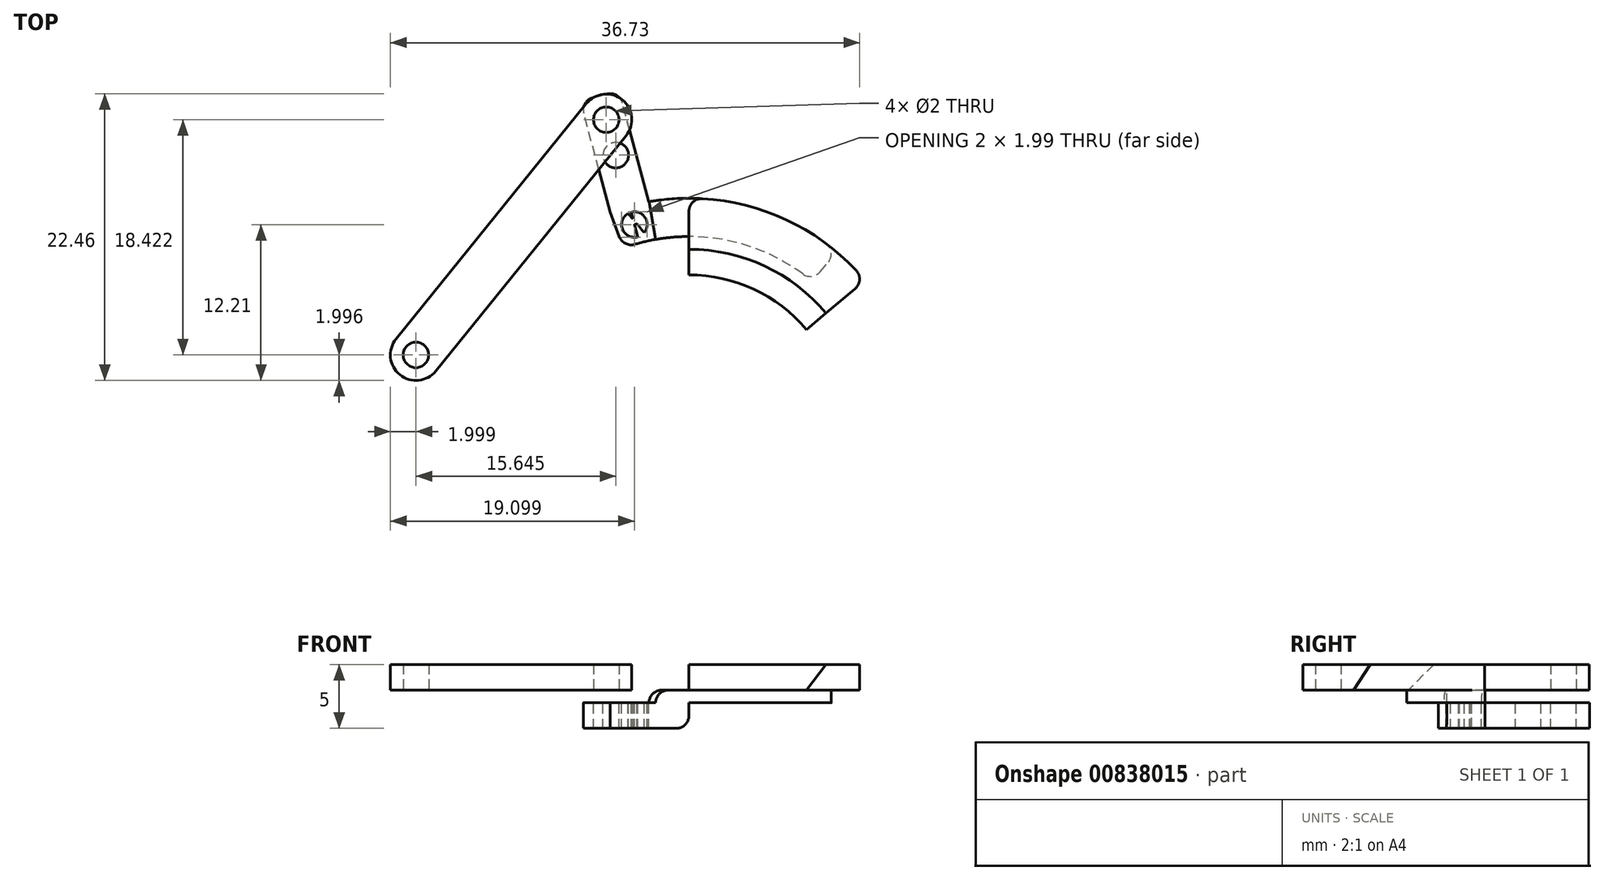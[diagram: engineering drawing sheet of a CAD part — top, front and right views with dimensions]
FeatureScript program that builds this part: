
annotation { "Feature Type Name" : "Feature", "Feature Type Description" : "" }
export const myFeature = defineFeature(function(context is Context, id is Id, definition is map)
    precondition{}
    {
        {
            var Q0;
            Q0=qCreatedBy(makeId("Top.planeOp"),FACE);
            var sketch = newSketch(context, id + "F0", { "sketchPlane" : qUnion([Q0])});
            skCircle(sketch, "E0", {"center": v(0, 0) * mm, "radius": 12 * mm});
            skLineSegment(sketch, "E1", {"start": v(0, 0) * mm, "end": v(0, 18) * mm});
            skLineSegment(sketch, "E2.1.0", {"start": v(0, 0) * mm, "end": v(-15.59, 9) * mm});
            skLineSegment(sketch, "E2.2.0", {"start": v(0, 0) * mm, "end": v(-15.59, -9) * mm});
            skLineSegment(sketch, "E2.3.0", {"start": v(0, 0) * mm, "end": v(0, -18) * mm});
            skLineSegment(sketch, "E2.4.0", {"start": v(0, 0) * mm, "end": v(15.59, -9) * mm});
            skLineSegment(sketch, "E2.5.0", {"start": v(0, 0) * mm, "end": v(15.59, 9) * mm});
            skLineSegment(sketch, "E3", {"start": v(0, 0) * mm, "end": v(-3.13, 17.73) * mm});
            skLineSegment(sketch, "E4.1.0", {"start": v(0, 0) * mm, "end": v(-16.91, 6.16) * mm});
            skLineSegment(sketch, "E4.2.0", {"start": v(0, 0) * mm, "end": v(-13.79, -11.57) * mm});
            skLineSegment(sketch, "E4.3.0", {"start": v(0, 0) * mm, "end": v(3.13, -17.73) * mm});
            skLineSegment(sketch, "E4.4.0", {"start": v(0, 0) * mm, "end": v(16.91, -6.16) * mm});
            skLineSegment(sketch, "E4.5.0", {"start": v(0, 0) * mm, "end": v(13.79, 11.57) * mm});
            skCircle(sketch, "E5", {"center": v(0, 0) * mm, "radius": 18 * mm});
            skLineSegment(sketch, "E6", {"start": v(0, 0) * mm, "end": v(-6.16, 16.91) * mm});
            skCircle(sketch, "E7", {"center": v(0, 0) * mm, "radius": 15 * mm});
            skLineSegment(sketch, "E8", {"start": v(0, 0) * mm, "end": v(11.57, 13.79) * mm});
            skSolve(sketch);
        }
        {
            var Q0;
            {var subQ0=sQuery(id+"F0.wireOp",EDGE,"E4.5.0");var subQ1=sQuery(id+"F0.wireOp",EDGE,"E0");var subQ2=makeQuery(id+"F0.imprint","INTERSECT",VERTEX,{"derivedFrom":[subQ1,subQ0]});Q0=makeQuery(id+"F0.imprint","IMPRINT",FACE,{"disambiguationData":[TD([[makeQuery(id+"F0.imprint","IMPRINT",EDGE,{"disambiguationData":[TD([[subQ2,-1.0]])],"derivedFrom":subQ1}),-1.0]])]});}
            var Q1;
            {var subQ0=sQuery(id+"F0.wireOp",EDGE,"E5");var subQ1=sQuery(id+"F0.wireOp",EDGE,"E1");var subQ2=makeQuery(id+"F0.imprint","INTERSECT",VERTEX,{"derivedFrom":[subQ1,subQ0]});Q1=makeQuery(id+"F0.imprint","IMPRINT",FACE,{"disambiguationData":[TD([[makeQuery(id+"F0.imprint","IMPRINT",EDGE,{"disambiguationData":[TD([[subQ2,1.0]])],"derivedFrom":subQ1}),-1.0]])]});}
            var Q2;
            {var subQ0=sQuery(id+"F0.wireOp",EDGE,"E8");var subQ1=sQuery(id+"F0.wireOp",EDGE,"E0");var subQ2=makeQuery(id+"F0.imprint","INTERSECT",VERTEX,{"derivedFrom":[subQ1,subQ0]});Q2=makeQuery(id+"F0.imprint","IMPRINT",FACE,{"disambiguationData":[TD([[makeQuery(id+"F0.imprint","IMPRINT",EDGE,{"disambiguationData":[TD([[subQ2,-1.0]])],"derivedFrom":subQ1}),-1.0]])]});}
            var Q3;
            {var subQ0=sQuery(id+"F0.wireOp",EDGE,"E5");var subQ1=sQuery(id+"F0.wireOp",EDGE,"E4.5.0");var subQ2=makeQuery(id+"F0.imprint","INTERSECT",VERTEX,{"derivedFrom":[subQ1,subQ0]});Q3=makeQuery(id+"F0.imprint","IMPRINT",FACE,{"disambiguationData":[TD([[makeQuery(id+"F0.imprint","IMPRINT",EDGE,{"disambiguationData":[TD([[subQ2,1.0]])],"derivedFrom":subQ1}),1.0]])]});}
            extrude(context, id + "F1", {"entities" : qUnion([Q0, Q1, Q2, Q3]), "depth" : 2 * mm, "offsetDistance" : 25 * mm});
        }
        {
            var Q0;
            {var subQ0=sQuery(id+"F0.wireOp",EDGE,"E5");var subQ1=sQuery(id+"F0.wireOp",EDGE,"E1");var subQ2=makeQuery(id+"F0.imprint","INTERSECT",VERTEX,{"derivedFrom":[subQ1,subQ0]});Q0=makeQuery(id+"F0.imprint","IMPRINT",FACE,{"disambiguationData":[TD([[makeQuery(id+"F0.imprint","IMPRINT",EDGE,{"disambiguationData":[TD([[subQ2,1.0]])],"derivedFrom":subQ1}),1.0]])]});}
            var Q1;
            {var subQ0=sQuery(id+"F0.wireOp",EDGE,"E5");var subQ1=sQuery(id+"F0.wireOp",EDGE,"E1");var subQ2=makeQuery(id+"F0.imprint","INTERSECT",VERTEX,{"derivedFrom":[subQ1,subQ0]});Q1=makeQuery(id+"F0.imprint","IMPRINT",FACE,{"disambiguationData":[TD([[makeQuery(id+"F0.imprint","IMPRINT",EDGE,{"disambiguationData":[TD([[subQ2,1.0]])],"derivedFrom":subQ1}),-1.0]])]});}
            extrude(context, id + "F2", {"entities" : qUnion([Q0, Q1]), "operationType" : NewBodyOperationType.ADD, "oppositeDirection" : true, "depth" : 1 * mm, "offsetDistance" : 25 * mm});
        }
        {
            var Q0;
            {var subQ0=sQuery(id+"F0.wireOp",EDGE,"E5");var subQ1=sQuery(id+"F0.wireOp",EDGE,"E3");var subQ2=makeQuery(id+"F0.imprint","INTERSECT",VERTEX,{"derivedFrom":[subQ1,subQ0]});Q0=makeQuery(id+"F0.imprint","IMPRINT",FACE,{"disambiguationData":[TD([[makeQuery(id+"F0.imprint","IMPRINT",EDGE,{"disambiguationData":[TD([[subQ2,1.0]])],"derivedFrom":subQ1}),1.0]])]});}
            var Q1;
            {var subQ0=sQuery(id+"F0.wireOp",EDGE,"E5");var subQ1=sQuery(id+"F0.wireOp",EDGE,"E1");var subQ2=makeQuery(id+"F0.imprint","INTERSECT",VERTEX,{"derivedFrom":[subQ1,subQ0]});Q1=makeQuery(id+"F0.imprint","IMPRINT",FACE,{"disambiguationData":[TD([[makeQuery(id+"F0.imprint","IMPRINT",EDGE,{"disambiguationData":[TD([[subQ2,1.0]])],"derivedFrom":subQ1}),1.0]])]});}
            extrude(context, id + "F3", {"entities" : qUnion([Q0, Q1]), "operationType" : NewBodyOperationType.ADD, "oppositeDirection" : true, "depth" : 3 * mm, "offsetDistance" : 25 * mm, "hasSecondDirection" : true, "secondDirectionOppositeDirection" : true, "secondDirectionDepth" : 1 * mm});
        }
        {
            var Q0;
            Q0=qCreatedBy(makeId("Top.planeOp"),FACE);
            var sketch = newSketch(context, id + "F4", { "sketchPlane" : qUnion([Q0])});
            skLineSegment(sketch, "E9", {"start": v(0, 0) * mm, "end": v(-6.47, 24.15) * mm});
            skCircle(sketch, "E10", {"center": v(0, 0) * mm, "radius": 16.5 * mm});
            skCircle(sketch, "E11", {"center": v(-4.27, 15.94) * mm, "radius": 1 * mm});
            skLineSegment(sketch, "E12", {"start": v(0, 0) * mm, "end": v(-24.15, 6.47) * mm});
            skCircle(sketch, "E13", {"center": v(-4.27, 15.94) * mm, "radius": 8.5 * mm});
            skCircle(sketch, "E14", {"center": v(-15.94, 4.27) * mm, "radius": 8.5 * mm});
            skLineSegment(sketch, "E15", {"start": v(-4.27, 15.94) * mm, "end": v(-11.63, 20.19) * mm});
            skLineSegment(sketch, "E16", {"start": v(-15.94, 4.27) * mm, "end": v(-23.3, 0.02) * mm});
            skCircle(sketch, "E17", {"center": v(-23.3, 0.02) * mm, "radius": 25 * mm});
            skCircle(sketch, "E18", {"center": v(-24.15, 6.47) * mm, "radius": 25 * mm});
            skCircle(sketch, "E19", {"center": v(-4.27, 15.94) * mm, "radius": 5.62 * mm});
            skLineSegment(sketch, "E20", {"start": v(-9.14, 18.75) * mm, "end": v(-8.2, 19.95) * mm});
            skLineSegment(sketch, "E21", {"start": v(-5.73, 21.37) * mm, "end": v(-4.22, 21.56) * mm});
            skCircle(sketch, "E22", {"center": v(-5.73, 21.37) * mm, "radius": 1 * mm});
            skCircle(sketch, "E23", {"center": v(-6.47, 24.15) * mm, "radius": 1 * mm});
            skLineSegment(sketch, "E24", {"start": v(0, 0) * mm, "end": v(-7.22, 26.96) * mm});
            skCircle(sketch, "E25", {"center": v(0, 0) * mm, "radius": 18 * mm});
            skLineSegment(sketch, "E26", {"start": v(-6.16, 16.91) * mm, "end": v(-8.49, 25.6) * mm});
            skLineSegment(sketch, "E27", {"start": v(-3.14, 17.72) * mm, "end": v(-5.47, 26.42) * mm});
            skLineSegment(sketch, "E28", {"start": v(-8.49, 25.6) * mm, "end": v(-5.47, 26.42) * mm});
            skCircle(sketch, "E29.1.0", {"center": v(-21.37, 5.73) * mm, "radius": 1 * mm});
            skCircle(sketch, "E29.2.0", {"center": v(-15.64, -15.64) * mm, "radius": 1 * mm});
            skCircle(sketch, "E29.3.0", {"center": v(5.73, -21.37) * mm, "radius": 1 * mm});
            skCircle(sketch, "E29.4.0", {"center": v(21.37, -5.73) * mm, "radius": 1 * mm});
            skCircle(sketch, "E29.5.0", {"center": v(15.64, 15.64) * mm, "radius": 1 * mm});
            skCircle(sketch, "E30", {"center": v(-21.37, 5.73) * mm, "radius": 1.69 * mm});
            skSolve(sketch);
        }
        {
            var Q0;
            {var subQ1=sQuery(id+"F4.wireOp",EDGE,"E27");var subQ3=sQuery(id+"F4.wireOp",EDGE,"E13");var subQ4=makeQuery(id+"F4.imprint","INTERSECT",VERTEX,{"derivedFrom":[subQ3,subQ1]});Q0=makeQuery(id+"F4.imprint","IMPRINT",FACE,{"disambiguationData":[TD([[makeQuery(id+"F4.imprint","IMPRINT",EDGE,{"disambiguationData":[TD([[subQ4,-1.0]])],"derivedFrom":subQ3}),-1.0]])]});}
            var Q1;
            {var subQ0=sQuery(id+"F4.wireOp",EDGE,"E28");var subQ1=sQuery(id+"F4.wireOp",EDGE,"E18");var subQ2=makeQuery(id+"F4.imprint","INTERSECT",VERTEX,{"derivedFrom":[subQ1,subQ0]});Q1=makeQuery(id+"F4.imprint","IMPRINT",FACE,{"disambiguationData":[TD([[makeQuery(id+"F4.imprint","IMPRINT",EDGE,{"disambiguationData":[TD([[subQ2,1.0]])],"derivedFrom":subQ1}),-1.0]])]});}
            var Q2;
            {var subQ3=sQuery(id+"F4.wireOp",EDGE,"E13");var subQ5=sQuery(id+"F4.wireOp",EDGE,"E23");var subQ6=makeQuery(id+"F4.imprint","INTERSECT",VERTEX,{"disambiguationData":[OD(1.0)],"derivedFrom":[subQ3,subQ5]});Q2=makeQuery(id+"F4.imprint","IMPRINT",FACE,{"disambiguationData":[TD([[makeQuery(id+"F4.imprint","IMPRINT",EDGE,{"disambiguationData":[TD([[subQ6,-1.0]])],"derivedFrom":subQ3}),-1.0]])]});}
            var Q3;
            {var subQ5=sQuery(id+"F4.wireOp",EDGE,"E23");var subQ6=sQuery(id+"F4.wireOp",EDGE,"E13");var subQ7=makeQuery(id+"F4.imprint","INTERSECT",VERTEX,{"disambiguationData":[OD(1.0)],"derivedFrom":[subQ6,subQ5]});Q3=makeQuery(id+"F4.imprint","IMPRINT",FACE,{"disambiguationData":[TD([[makeQuery(id+"F4.imprint","IMPRINT",EDGE,{"disambiguationData":[TD([[subQ7,-1.0]])],"derivedFrom":subQ6}),1.0]])]});}
            var Q4;
            {var subQ3=sQuery(id+"F4.wireOp",EDGE,"E25");var subQ5=sQuery(id+"F4.wireOp",EDGE,"E17");var subQ6=makeQuery(id+"F4.imprint","INTERSECT",VERTEX,{"disambiguationData":[OD(1.0)],"derivedFrom":[subQ5,subQ3]});Q4=makeQuery(id+"F4.imprint","IMPRINT",FACE,{"disambiguationData":[TD([[makeQuery(id+"F4.imprint","IMPRINT",EDGE,{"disambiguationData":[TD([[subQ6,-1.0]])],"derivedFrom":subQ5}),-1.0]])]});}
            var Q5;
            {var subQ0=sQuery(id+"F4.wireOp",EDGE,"E25");var subQ1=sQuery(id+"F4.wireOp",EDGE,"E15");var subQ2=makeQuery(id+"F4.imprint","INTERSECT",VERTEX,{"derivedFrom":[subQ1,subQ0]});Q5=makeQuery(id+"F4.imprint","IMPRINT",FACE,{"disambiguationData":[TD([[makeQuery(id+"F4.imprint","IMPRINT",EDGE,{"disambiguationData":[TD([[subQ2,-1.0]])],"derivedFrom":subQ1}),-1.0]])]});}
            var Q6;
            {var subQ1=sQuery(id+"F4.wireOp",EDGE,"E22");var subQ5=sQuery(id+"F4.wireOp",EDGE,"E21");var subQ6=makeQuery(id+"F4.imprint","INTERSECT",VERTEX,{"derivedFrom":[subQ5,subQ1]});Q6=makeQuery(id+"F4.imprint","IMPRINT",FACE,{"disambiguationData":[TD([[makeQuery(id+"F4.imprint","IMPRINT",EDGE,{"disambiguationData":[TD([[subQ6,1.0]])],"derivedFrom":subQ1}),-1.0]])]});}
            var Q7;
            {var subQ1=sQuery(id+"F4.wireOp",EDGE,"E13");var subQ7=sQuery(id+"F4.wireOp",EDGE,"E27");var subQ9=makeQuery(id+"F4.imprint","INTERSECT",VERTEX,{"derivedFrom":[subQ1,subQ7]});Q7=makeQuery(id+"F4.imprint","IMPRINT",FACE,{"disambiguationData":[TD([[makeQuery(id+"F4.imprint","IMPRINT",EDGE,{"disambiguationData":[TD([[subQ9,-1.0]])],"derivedFrom":subQ1}),1.0]])]});}
            var Q8;
            {var subQ5=sQuery(id+"F4.wireOp",EDGE,"E22");var subQ6=sQuery(id+"F4.wireOp",EDGE,"E19");var subQ7=makeQuery(id+"F4.imprint","INTERSECT",VERTEX,{"disambiguationData":[OD(0.0)],"derivedFrom":[subQ6,subQ5]});Q8=makeQuery(id+"F4.imprint","IMPRINT",FACE,{"disambiguationData":[TD([[makeQuery(id+"F4.imprint","IMPRINT",EDGE,{"disambiguationData":[TD([[subQ7,-1.0]])],"derivedFrom":subQ5}),-1.0]])]});}
            var Q9;
            {var subQ1=sQuery(id+"F4.wireOp",EDGE,"E19");var subQ3=sQuery(id+"F4.wireOp",EDGE,"E22");var subQ4=makeQuery(id+"F4.imprint","INTERSECT",VERTEX,{"disambiguationData":[OD(0.0)],"derivedFrom":[subQ1,subQ3]});Q9=makeQuery(id+"F4.imprint","IMPRINT",FACE,{"disambiguationData":[TD([[makeQuery(id+"F4.imprint","IMPRINT",EDGE,{"disambiguationData":[TD([[subQ4,1.0]])],"derivedFrom":subQ3}),-1.0]])]});}
            var Q10;
            {var subQ1=sQuery(id+"F4.wireOp",EDGE,"E18");var subQ3=sQuery(id+"F4.wireOp",EDGE,"E27");var subQ4=makeQuery(id+"F4.imprint","INTERSECT",VERTEX,{"derivedFrom":[subQ1,subQ3]});Q10=makeQuery(id+"F4.imprint","IMPRINT",FACE,{"disambiguationData":[TD([[makeQuery(id+"F4.imprint","IMPRINT",EDGE,{"disambiguationData":[TD([[subQ4,-1.0]])],"derivedFrom":subQ3}),1.0]])]});}
            var Q11;
            {var subQ0=sQuery(id+"F4.wireOp",EDGE,"E25");var subQ1=sQuery(id+"F4.wireOp",EDGE,"E15");var subQ2=makeQuery(id+"F4.imprint","INTERSECT",VERTEX,{"derivedFrom":[subQ1,subQ0]});Q11=makeQuery(id+"F4.imprint","IMPRINT",FACE,{"disambiguationData":[TD([[makeQuery(id+"F4.imprint","IMPRINT",EDGE,{"disambiguationData":[TD([[subQ2,-1.0]])],"derivedFrom":subQ1}),1.0]])]});}
            extrude(context, id + "F5", {"entities" : qUnion([Q0, Q1, Q2, Q3, Q4, Q5, Q6, Q7, Q8, Q9, Q10, Q11]), "operationType" : NewBodyOperationType.ADD, "oppositeDirection" : true, "depth" : 3 * mm, "offsetDistance" : 25 * mm, "hasSecondDirection" : true, "secondDirectionOppositeDirection" : true, "secondDirectionDepth" : 1 * mm});
        }
        {
            var Q0;
            {var subQ0=sQuery(id+"F4.wireOp",EDGE,"E24");var subQ1=sQuery(id+"F4.wireOp",EDGE,"E11");var subQ2=makeQuery(id+"F4.imprint","INTERSECT",VERTEX,{"disambiguationData":[OD(0.0)],"derivedFrom":[subQ1,subQ0]});Q0=makeQuery(id+"F4.imprint","IMPRINT",FACE,{"disambiguationData":[TD([[makeQuery(id+"F4.imprint","IMPRINT",EDGE,{"disambiguationData":[TD([[subQ2,-1.0]])],"derivedFrom":subQ1}),1.0]])]});}
            var Q1;
            {var subQ0=sQuery(id+"F4.wireOp",EDGE,"E17");var subQ1=sQuery(id+"F4.wireOp",EDGE,"E11");var subQ2=makeQuery(id+"F4.imprint","INTERSECT",VERTEX,{"disambiguationData":[OD(0.0)],"derivedFrom":[subQ1,subQ0]});Q1=makeQuery(id+"F4.imprint","IMPRINT",FACE,{"disambiguationData":[TD([[makeQuery(id+"F4.imprint","IMPRINT",EDGE,{"disambiguationData":[TD([[subQ2,-1.0]])],"derivedFrom":subQ1}),1.0]])]});}
            var Q2;
            {var subQ1=sQuery(id+"F4.wireOp",EDGE,"E10");var subQ3=sQuery(id+"F4.wireOp",EDGE,"E11");var subQ4=makeQuery(id+"F4.imprint","INTERSECT",VERTEX,{"disambiguationData":[OD(1.0)],"derivedFrom":[subQ1,subQ3]});Q2=makeQuery(id+"F4.imprint","IMPRINT",FACE,{"disambiguationData":[TD([[makeQuery(id+"F4.imprint","IMPRINT",EDGE,{"disambiguationData":[TD([[subQ4,1.0]])],"derivedFrom":subQ3}),1.0]])]});}
            var Q3;
            {var subQ1=sQuery(id+"F4.wireOp",EDGE,"E10");var subQ3=sQuery(id+"F4.wireOp",EDGE,"E11");var subQ4=makeQuery(id+"F4.imprint","INTERSECT",VERTEX,{"disambiguationData":[OD(1.0)],"derivedFrom":[subQ1,subQ3]});Q3=makeQuery(id+"F4.imprint","IMPRINT",FACE,{"disambiguationData":[TD([[makeQuery(id+"F4.imprint","IMPRINT",EDGE,{"disambiguationData":[TD([[subQ4,-1.0]])],"derivedFrom":subQ3}),1.0]])]});}
            var Q4;
            {var subQ0=sQuery(id+"F4.wireOp",EDGE,"E24");var subQ5=sQuery(id+"F4.wireOp",EDGE,"E11");var subQ6=makeQuery(id+"F4.imprint","INTERSECT",VERTEX,{"disambiguationData":[OD(1.0)],"derivedFrom":[subQ5,subQ0]});Q4=makeQuery(id+"F4.imprint","IMPRINT",FACE,{"disambiguationData":[TD([[makeQuery(id+"F4.imprint","IMPRINT",EDGE,{"disambiguationData":[TD([[subQ6,-1.0]])],"derivedFrom":subQ5}),1.0]])]});}
            var Q5;
            {var subQ0=sQuery(id+"F4.wireOp",EDGE,"E11");var subQ1=sQuery(id+"F4.wireOp",EDGE,"E10");var subQ2=makeQuery(id+"F4.imprint","INTERSECT",VERTEX,{"disambiguationData":[OD(0.0)],"derivedFrom":[subQ1,subQ0]});Q5=makeQuery(id+"F4.imprint","IMPRINT",FACE,{"disambiguationData":[TD([[makeQuery(id+"F4.imprint","IMPRINT",EDGE,{"disambiguationData":[TD([[subQ2,-1.0]])],"derivedFrom":subQ1}),1.0]])]});}
            var Q6;
            {var subQ1=sQuery(id+"F4.wireOp",EDGE,"E10");var subQ3=sQuery(id+"F4.wireOp",EDGE,"E17");var subQ4=makeQuery(id+"F4.imprint","INTERSECT",VERTEX,{"disambiguationData":[OD(0.0)],"derivedFrom":[subQ1,subQ3]});Q6=makeQuery(id+"F4.imprint","IMPRINT",FACE,{"disambiguationData":[TD([[makeQuery(id+"F4.imprint","IMPRINT",EDGE,{"disambiguationData":[TD([[subQ4,-1.0]])],"derivedFrom":subQ3}),1.0]])]});}
            var Q7;
            {var subQ0=sQuery(id+"F4.wireOp",EDGE,"E11");var subQ1=sQuery(id+"F4.wireOp",EDGE,"E10");var subQ2=makeQuery(id+"F4.imprint","INTERSECT",VERTEX,{"disambiguationData":[OD(0.0)],"derivedFrom":[subQ1,subQ0]});Q7=makeQuery(id+"F4.imprint","IMPRINT",FACE,{"disambiguationData":[TD([[makeQuery(id+"F4.imprint","IMPRINT",EDGE,{"disambiguationData":[TD([[subQ2,-1.0]])],"derivedFrom":subQ1}),-1.0]])]});}
            extrude(context, id + "F6", {"entities" : qUnion([Q0, Q1, Q2, Q3, Q4, Q5, Q6, Q7]), "operationType" : NewBodyOperationType.REMOVE, "oppositeDirection" : true, "depth" : 25 * mm, "offsetDistance" : 25 * mm});
        }
        {
            var Q0;
            Q0=makeQuery(id+"F1.opExtrude","CAP_EDGE",EDGE,{"disambiguationData":[OSD([sQuery(id+"F0.wireOp",EDGE,"E0")])],"isStart":false});
            chamfer(context, id + "F7", {"entities" : qUnion([Q0]), "width" : 2 * mm, "tangentPropagation" : true});
        }
        {
            var Q0;
            Q0=makeQuery(id+"F1.opExtrude","SWEPT_EDGE",EDGE,{"disambiguationData":[OSD([sQuery(id+"F0.wireOp",EDGE,"E4.5.0"),sQuery(id+"F0.wireOp",EDGE,"E5")])]});
            var Q1;
            Q1=makeQuery(id+"F2.opExtrude","SWEPT_EDGE",EDGE,{"disambiguationData":[OSD([sQuery(id+"F0.wireOp",EDGE,"E7"),sQuery(id+"F0.wireOp",EDGE,"E8")])]});
            var Q2;
            Q2=makeQuery(id+"F2.opExtrude","SWEPT_EDGE",EDGE,{"disambiguationData":[OSD([sQuery(id+"F0.wireOp",EDGE,"E5"),sQuery(id+"F0.wireOp",EDGE,"E8")])]});
            var Q3;
            Q3=makeQuery(id+"F3.opExtrude","CAP_EDGE",EDGE,{"disambiguationData":[OSD([sQuery(id+"F0.wireOp",EDGE,"E1")])],"isStart":true});
            var Q4;
            Q4=makeQuery(id+"F3.opExtrude","CAP_EDGE",EDGE,{"disambiguationData":[OSD([sQuery(id+"F0.wireOp",EDGE,"E1")])],"isStart":false});
            var Q5;
            Q5=makeQuery(id+"F2.opExtrude","CAP_EDGE",EDGE,{"disambiguationData":[OSD([sQuery(id+"F0.wireOp",EDGE,"E3")])],"isStart":true});
            var Q6;
            Q6=makeQuery(id+"F3.opExtrude","SWEPT_EDGE",EDGE,{"disambiguationData":[OSD([sQuery(id+"F0.wireOp",EDGE,"E6"),sQuery(id+"F0.wireOp",EDGE,"E7")])]});
            var Q7;
            Q7=makeQuery(id+"F5.opExtrude","SWEPT_EDGE",EDGE,{"disambiguationData":[OSD([sQuery(id+"F4.wireOp",EDGE,"E26"),sQuery(id+"F4.wireOp",EDGE,"E28")])]});
            var Q8;
            Q8=makeQuery(id+"F5.opExtrude","SWEPT_EDGE",EDGE,{"disambiguationData":[OSD([sQuery(id+"F4.wireOp",EDGE,"E27"),sQuery(id+"F4.wireOp",EDGE,"E28")])]});
            var Q9;
            Q9=makeQuery(id+"F1.opExtrude","SWEPT_EDGE",EDGE,{"disambiguationData":[OSD([sQuery(id+"F0.wireOp",EDGE,"E1"),sQuery(id+"F0.wireOp",EDGE,"E5")])]});
            fillet(context, id + "F8", {"entities" : qUnion([Q0, Q1, Q2, Q3, Q4, Q5, Q6, Q7, Q8, Q9]), "radius" : 1 * mm, "tangentPropagation" : true, "allowEdgeOverflow" : false});
        }
        {
            var Q0;
            Q0=qCreatedBy(makeId("Top.planeOp"),FACE);
            var sketch = newSketch(context, id + "F9", { "sketchPlane" : qUnion([Q0])});
            skLineSegment(sketch, "E31", {"start": v(0, 0) * mm, "end": v(-6.47, 24.15) * mm});
            skLineSegment(sketch, "E32", {"start": v(0, 0) * mm, "end": v(-21.37, 5.73) * mm});
            skCircle(sketch, "E33", {"center": v(-21.37, 5.73) * mm, "radius": 1 * mm});
            skCircle(sketch, "E34", {"center": v(-6.47, 24.15) * mm, "radius": 1 * mm});
            skCircle(sketch, "E35", {"center": v(-21.37, 5.73) * mm, "radius": 2 * mm});
            skCircle(sketch, "E36", {"center": v(-6.47, 24.15) * mm, "radius": 2 * mm});
            skLineSegment(sketch, "E37", {"start": v(-22.93, 6.98) * mm, "end": v(-8.03, 25.4) * mm});
            skLineSegment(sketch, "E38", {"start": v(-19.82, 4.47) * mm, "end": v(-4.92, 22.9) * mm});
            skSolve(sketch);
        }
        {
            var Q0;
            Q0=makeQuery(id+"F9.imprint","IMPRINT",FACE,{"disambiguationData":[TD([[makeQuery(id+"F9.imprint","IMPRINT",EDGE,{"derivedFrom":sQuery(id+"F9.wireOp",EDGE,"E34")}),-1.0]])]});
            var Q1;
            {var subQ0=sQuery(id+"F9.wireOp",EDGE,"E37");Q1=makeQuery(id+"F9.imprint","IMPRINT",FACE,{"disambiguationData":[TD([[makeQuery(id+"F9.imprint","IMPRINT",EDGE,{"derivedFrom":subQ0}),-1.0]])]});}
            var Q2;
            Q2=makeQuery(id+"F9.imprint","IMPRINT",FACE,{"disambiguationData":[TD([[makeQuery(id+"F9.imprint","IMPRINT",EDGE,{"derivedFrom":sQuery(id+"F9.wireOp",EDGE,"E33")}),-1.0]])]});
            var Q3;
            {var subQ0=sQuery(id+"F9.wireOp",EDGE,"E38");var subQ1=sQuery(id+"F9.wireOp",EDGE,"E32");var subQ2=makeQuery(id+"F9.imprint","INTERSECT",VERTEX,{"derivedFrom":[subQ1,subQ0]});Q3=makeQuery(id+"F9.imprint","IMPRINT",FACE,{"disambiguationData":[TD([[makeQuery(id+"F9.imprint","IMPRINT",EDGE,{"disambiguationData":[TD([[subQ2,-1.0]])],"derivedFrom":subQ1}),1.0]])]});}
            var Q4;
            {var subQ0=sQuery(id+"F9.wireOp",EDGE,"E38");var subQ1=sQuery(id+"F9.wireOp",EDGE,"E31");var subQ2=makeQuery(id+"F9.imprint","INTERSECT",VERTEX,{"derivedFrom":[subQ1,subQ0]});Q4=makeQuery(id+"F9.imprint","IMPRINT",FACE,{"disambiguationData":[TD([[makeQuery(id+"F9.imprint","IMPRINT",EDGE,{"disambiguationData":[TD([[subQ2,-1.0]])],"derivedFrom":subQ1}),-1.0]])]});}
            extrude(context, id + "F10", {"entities" : qUnion([Q0, Q1, Q2, Q3, Q4]), "depth" : 2 * mm, "offsetDistance" : 25 * mm});
        }
    });
